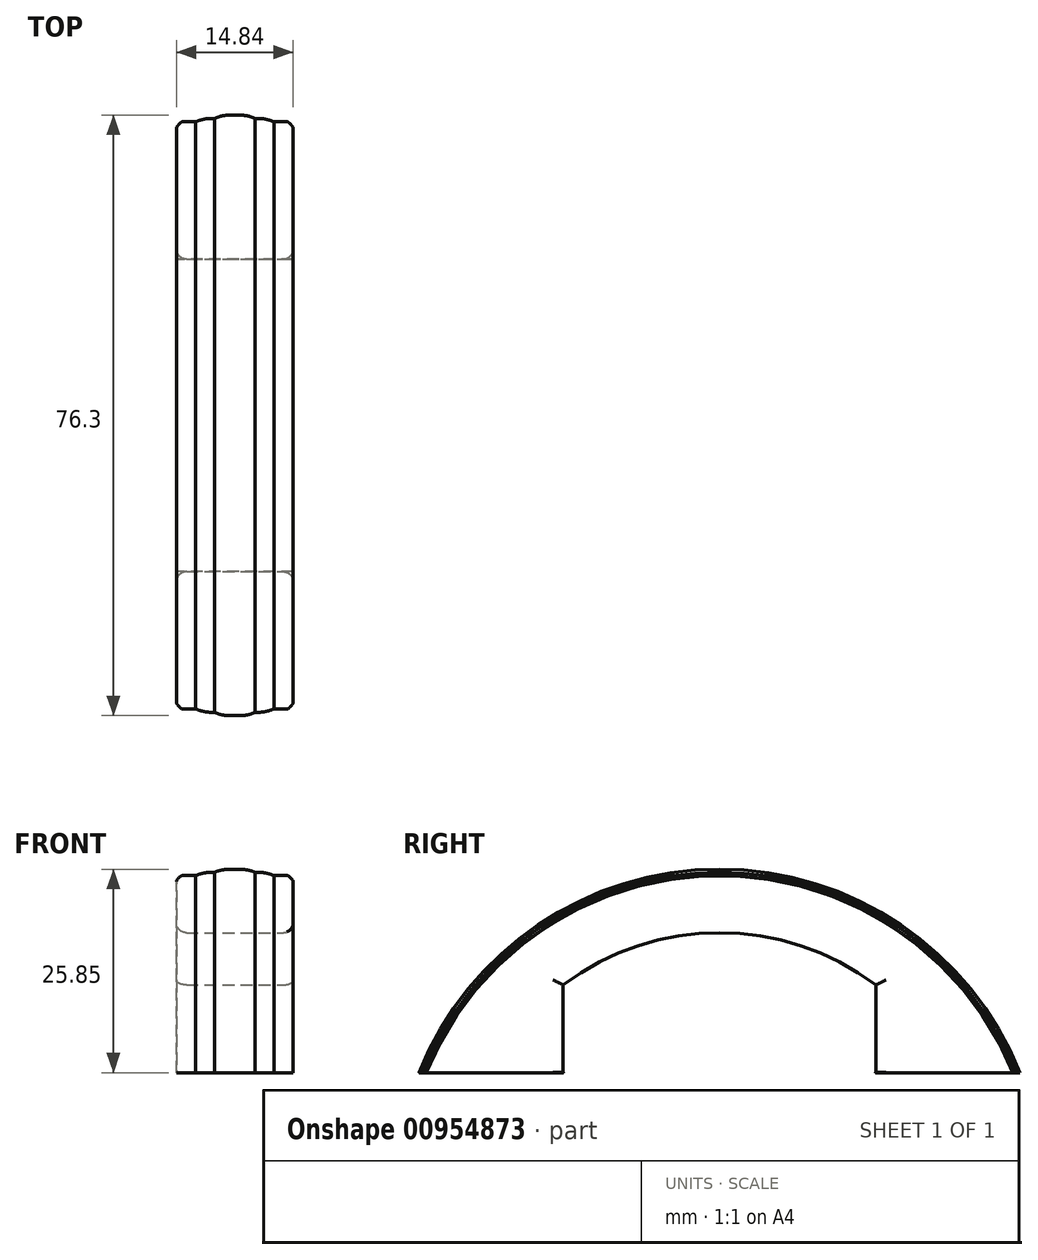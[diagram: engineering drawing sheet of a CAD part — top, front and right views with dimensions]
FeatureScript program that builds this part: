
annotation { "Feature Type Name" : "Feature", "Feature Type Description" : "" }
export const myFeature = defineFeature(function(context is Context, id is Id, definition is map)
    precondition{}
    {
        {
            var Q0;
            Q0=qCreatedBy(makeId("Front.planeOp"),FACE);
            var sketch = newSketch(context, id + "F0", { "sketchPlane" : qUnion([Q0])});
            skLineSegment(sketch, "E0", {"start": v(-55.67, 0) * mm, "end": v(68.03, 0) * mm, "construction": true});
            skLineSegment(sketch, "E1", {"start": v(-7.42, 0) * mm, "end": v(-7.42, 40.28) * mm});
            skLineSegment(sketch, "E2", {"start": v(-7.42, 40.28) * mm, "end": v(-4.96, 40.28) * mm});
            skLineSegment(sketch, "E3", {"start": v(-4.96, 40.28) * mm, "end": v(-4.96, 40.68) * mm});
            skLineSegment(sketch, "E4", {"start": v(-4.96, 40.68) * mm, "end": v(-2.58, 40.68) * mm});
            skLineSegment(sketch, "E5", {"start": v(-2.58, 40.68) * mm, "end": v(-2.58, 41.08) * mm});
            skLineSegment(sketch, "E6", {"start": v(-2.58, 41.08) * mm, "end": v(2.58, 41.08) * mm});
            skLineSegment(sketch, "E7", {"start": v(2.58, 41.08) * mm, "end": v(2.58, 40.68) * mm});
            skLineSegment(sketch, "E8", {"start": v(2.58, 40.68) * mm, "end": v(4.96, 40.68) * mm});
            skLineSegment(sketch, "E9", {"start": v(4.96, 40.68) * mm, "end": v(4.96, 40.28) * mm});
            skLineSegment(sketch, "E10", {"start": v(4.96, 40.28) * mm, "end": v(7.42, 40.28) * mm});
            skLineSegment(sketch, "E11", {"start": v(7.42, 40.28) * mm, "end": v(7.42, 0) * mm});
            skLineSegment(sketch, "E12", {"start": v(7.42, 0) * mm, "end": v(-7.42, 0) * mm});
            skLineSegment(sketch, "E13", {"start": v(0, 0) * mm, "end": v(0, 47.43) * mm, "construction": true});
            skSolve(sketch);
        }
        {
            var Q0;
            Q0=makeQuery(id+"F0.imprint","IMPRINT",FACE,{"disambiguationData":[TD([[makeQuery(id+"F0.imprint","IMPRINT",EDGE,{"derivedFrom":sQuery(id+"F0.wireOp",EDGE,"E1")}),-1.0]])]});
            var Q1;
            Q1=sQuery(id+"F0.wireOp",EDGE,"E0");
            revolve(context, id + "F1", {"surfaceOperationType" : NewSurfaceOperationType.NEW, "entities" : qUnion([Q0]), "axis" : qUnion([Q1]), "revolveType" : RevolveType.FULL});
        }
        {
            var Q0;
            Q0=makeQuery(id+"F1.opRevolve","SWEPT_EDGE",EDGE,{"disambiguationData":[OSD([sQuery(id+"F0.wireOp",EDGE,"E10"),sQuery(id+"F0.wireOp",EDGE,"E11")])]});
            var Q1;
            Q1=makeQuery(id+"F1.opRevolve","SWEPT_EDGE",EDGE,{"disambiguationData":[OSD([sQuery(id+"F0.wireOp",EDGE,"E1"),sQuery(id+"F0.wireOp",EDGE,"E2")])]});
            fillet(context, id + "F2", {"entities" : qUnion([Q0, Q1]), "radius" : 0.76 * mm, "tangentPropagation" : true, "rho" : 0.2, "crossSection" : FilletCrossSection.CONIC, "allowEdgeOverflow" : false});
        }
        {
            var Q0;
            Q0=makeQuery(id+"F1.opRevolve","SWEPT_EDGE",EDGE,{"disambiguationData":[OSD([sQuery(id+"F0.wireOp",EDGE,"E8"),sQuery(id+"F0.wireOp",EDGE,"E9")])]});
            var Q1;
            Q1=makeQuery(id+"F1.opRevolve","SWEPT_EDGE",EDGE,{"disambiguationData":[OSD([sQuery(id+"F0.wireOp",EDGE,"E3"),sQuery(id+"F0.wireOp",EDGE,"E4")])]});
            fillet(context, id + "F3", {"entities" : qUnion([Q0, Q1]), "radius" : 5.08 * mm, "tangentPropagation" : true, "allowEdgeOverflow" : false});
        }
        {
            var Q0;
            Q0=makeQuery(id+"F1.opRevolve","SWEPT_EDGE",EDGE,{"disambiguationData":[OSD([sQuery(id+"F0.wireOp",EDGE,"E6"),sQuery(id+"F0.wireOp",EDGE,"E7")])]});
            var Q1;
            Q1=makeQuery(id+"F1.opRevolve","SWEPT_EDGE",EDGE,{"disambiguationData":[OSD([sQuery(id+"F0.wireOp",EDGE,"E5"),sQuery(id+"F0.wireOp",EDGE,"E6")])]});
            fillet(context, id + "F4", {"entities" : qUnion([Q0, Q1]), "radius" : 5.08 * mm, "tangentPropagation" : true, "allowEdgeOverflow" : false});
        }
        {
            var Q0;
            Q0=qCreatedBy(makeId("Right.planeOp"),FACE);
            var sketch = newSketch(context, id + "F5", { "sketchPlane" : qUnion([Q0])});
            skCircle(sketch, "E14", {"center": v(0, 0) * mm, "radius": 25 * mm});
            skSolve(sketch);
        }
        {
            var Q0;
            Q0=qSketchRegion(id+"F5",true);
            extrude(context, id + "F6", {"entities" : qUnion([Q0]), "operationType" : NewBodyOperationType.REMOVE, "endBound" : BoundingType.THROUGH_ALL, "depth" : 25.4 * mm, "offsetDistance" : 25.4 * mm, "hasSecondDirection" : true, "secondDirectionBound" : SecondDirectionBoundingType.THROUGH_ALL, "secondDirectionOppositeDirection" : true, "secondDirectionDepth" : 25.4 * mm});
        }
        {
            var Q0;
            Q0=qCreatedBy(makeId("Right.planeOp"),FACE);
            var sketch = newSketch(context, id + "F7", { "sketchPlane" : qUnion([Q0])});
            skLineSegment(sketch, "E15", {"start": v(0, 15.23) * mm, "end": v(-38.1, 15.23) * mm, "construction": true});
            skLineSegment(sketch, "E16.MirrorCS", {"start": v(0, 15.23) * mm, "end": v(38.1, 15.23) * mm, "construction": true});
            skLineSegment(sketch, "E17", {"start": v(-59.25, 15.23) * mm, "end": v(65.7, 15.23) * mm});
            skLineSegment(sketch, "E18", {"start": v(65.7, 15.23) * mm, "end": v(65.7, -43.9) * mm});
            skLineSegment(sketch, "E19", {"start": v(65.7, -43.9) * mm, "end": v(-59.25, -43.9) * mm});
            skLineSegment(sketch, "E20", {"start": v(-59.25, -43.9) * mm, "end": v(-59.25, 15.23) * mm});
            skSolve(sketch);
        }
        {
            var Q0;
            Q0=qSketchRegion(id+"F7",true);
            extrude(context, id + "F8", {"entities" : qUnion([Q0]), "operationType" : NewBodyOperationType.REMOVE, "endBound" : BoundingType.THROUGH_ALL, "oppositeDirection" : true, "depth" : 25.4 * mm, "offsetDistance" : 25.4 * mm, "hasSecondDirection" : true, "secondDirectionBound" : SecondDirectionBoundingType.THROUGH_ALL, "secondDirectionOppositeDirection" : false, "secondDirectionDepth" : 25.4 * mm});
        }
        {
            var Q0;
            Q0=qCreatedBy(makeId("Right.planeOp"),FACE);
            var sketch = newSketch(context, id + "F9", { "sketchPlane" : qUnion([Q0])});
            skLineSegment(sketch, "E21", {"start": v(-19.86, 15.26) * mm, "end": v(-19.86, 26.38) * mm});
            skLineSegment(sketch, "E22.MirrorCS", {"start": v(19.86, 15.26) * mm, "end": v(19.86, 26.38) * mm});
            skArc(sketch, "E23", {"start": v(-19.86, 26.38) * mm, "mid": v(0, 33.01) * mm, "end": v(19.86, 26.38) * mm});
            skLineSegment(sketch, "E24", {"start": v(-19.86, 15.26) * mm, "end": v(19.86, 15.26) * mm});
            skSolve(sketch);
        }
        {
            var Q0;
            Q0 = qSketchRegion(id + "F9", true);
            extrude(context, id + "F10", {"entities" : qUnion([Q0]), "operationType" : NewBodyOperationType.REMOVE, "endBound" : BoundingType.THROUGH_ALL, "oppositeDirection" : true, "depth" : 25.4 * mm, "offsetDistance" : 25.4 * mm, "hasSecondDirection" : true, "secondDirectionBound" : SecondDirectionBoundingType.THROUGH_ALL, "secondDirectionOppositeDirection" : false, "secondDirectionDepth" : 25.4 * mm});
        }
        {
            var Q0;
            Q0=makeQuery(id+"F10.boolean.opBoolean","INTERSECT",EDGE,{"derivedFrom":[makeQuery(id+"F1.opRevolve","SWEPT_FACE",FACE,{"disambiguationData":[OSD([sQuery(id+"F0.wireOp",EDGE,"E11")])]}),makeQuery(id+"F10.opExtrude","SWEPT_FACE",FACE,{"disambiguationData":[OSD([sQuery(id+"F9.wireOp",EDGE,"E23")])]})]});
            var Q1;
            Q1=makeQuery(id+"F10.boolean.opBoolean","INTERSECT",EDGE,{"derivedFrom":[makeQuery(id+"F1.opRevolve","SWEPT_FACE",FACE,{"disambiguationData":[OSD([sQuery(id+"F0.wireOp",EDGE,"E11")])]}),makeQuery(id+"F10.opExtrude","SWEPT_FACE",FACE,{"disambiguationData":[OSD([sQuery(id+"F9.wireOp",EDGE,"E21")])]})]});
            var Q2;
            Q2=makeQuery(id+"F10.boolean.opBoolean","INTERSECT",EDGE,{"derivedFrom":[makeQuery(id+"F1.opRevolve","SWEPT_FACE",FACE,{"disambiguationData":[OSD([sQuery(id+"F0.wireOp",EDGE,"E11")])]}),makeQuery(id+"F10.opExtrude","SWEPT_FACE",FACE,{"disambiguationData":[OSD([sQuery(id+"F9.wireOp",EDGE,"E22.MirrorCS")])]})]});
            var Q3;
            Q3=makeQuery(id+"F10.boolean.opBoolean","INTERSECT",EDGE,{"derivedFrom":[makeQuery(id+"F1.opRevolve","SWEPT_FACE",FACE,{"disambiguationData":[OSD([sQuery(id+"F0.wireOp",EDGE,"E1")])]}),makeQuery(id+"F10.opExtrude","SWEPT_FACE",FACE,{"disambiguationData":[OSD([sQuery(id+"F9.wireOp",EDGE,"E23")])]})]});
            var Q4;
            Q4=makeQuery(id+"F10.boolean.opBoolean","INTERSECT",EDGE,{"derivedFrom":[makeQuery(id+"F1.opRevolve","SWEPT_FACE",FACE,{"disambiguationData":[OSD([sQuery(id+"F0.wireOp",EDGE,"E1")])]}),makeQuery(id+"F10.opExtrude","SWEPT_FACE",FACE,{"disambiguationData":[OSD([sQuery(id+"F9.wireOp",EDGE,"E21")])]})]});
            var Q5;
            Q5=makeQuery(id+"F10.boolean.opBoolean","INTERSECT",EDGE,{"derivedFrom":[makeQuery(id+"F1.opRevolve","SWEPT_FACE",FACE,{"disambiguationData":[OSD([sQuery(id+"F0.wireOp",EDGE,"E1")])]}),makeQuery(id+"F10.opExtrude","SWEPT_FACE",FACE,{"disambiguationData":[OSD([sQuery(id+"F9.wireOp",EDGE,"E22.MirrorCS")])]})]});
            fillet(context, id + "F11", {"entities" : qUnion([Q0, Q1, Q2, Q3, Q4, Q5]), "radius" : 1.27 * mm, "tangentPropagation" : true, "allowEdgeOverflow" : false});
        }
    });
